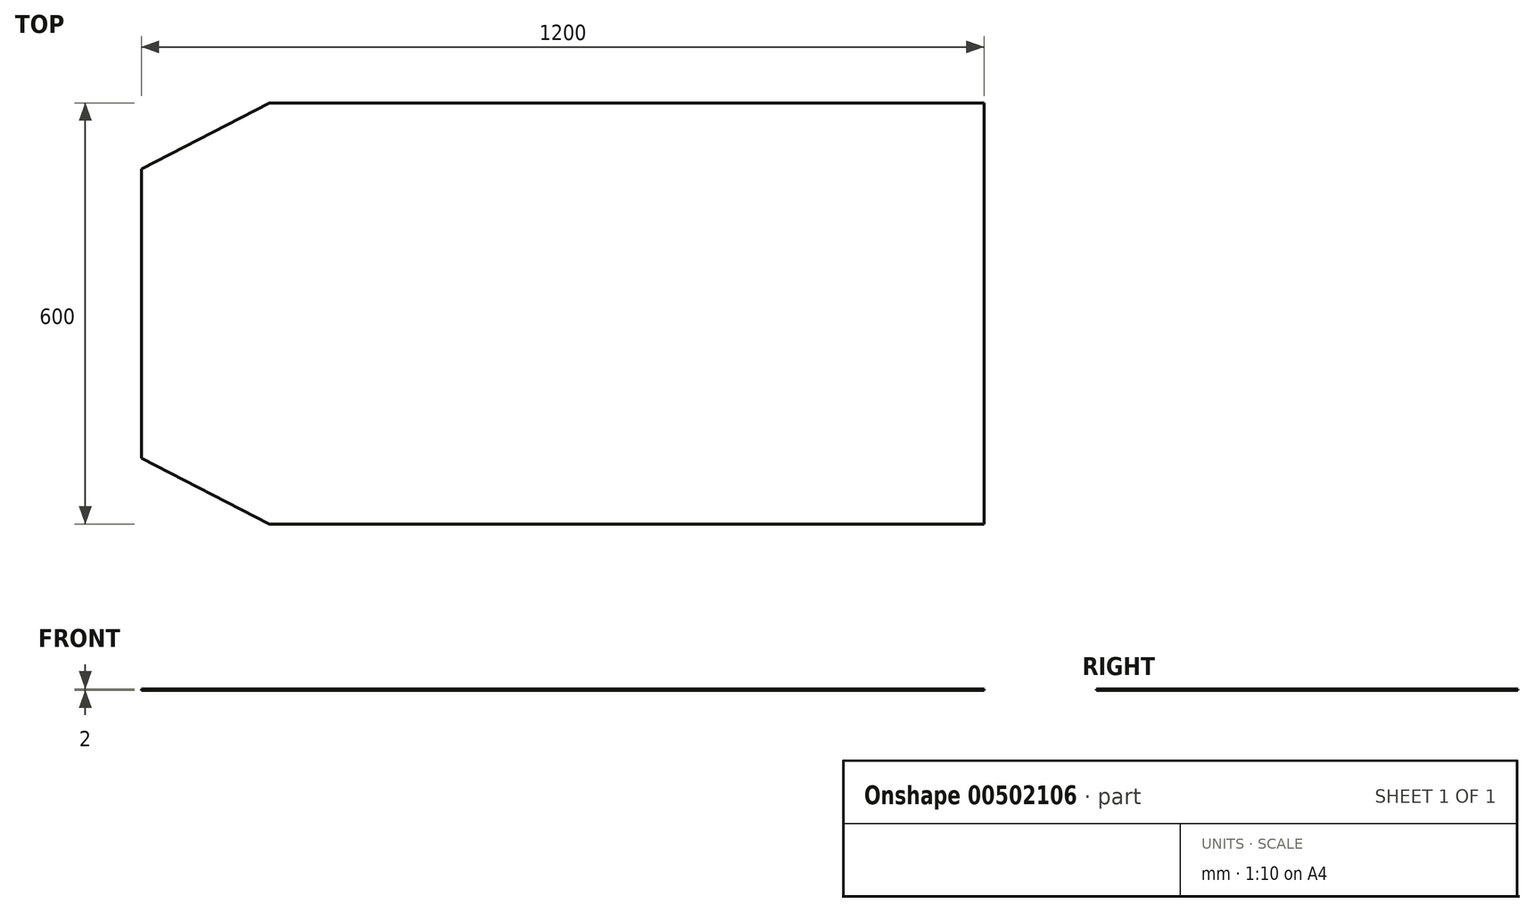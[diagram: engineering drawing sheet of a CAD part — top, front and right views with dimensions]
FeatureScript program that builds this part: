
annotation { "Feature Type Name" : "Feature", "Feature Type Description" : "" }
export const myFeature = defineFeature(function(context is Context, id is Id, definition is map)
    precondition{}
    {
        {
            var Q0;
            Q0=qCreatedBy(makeId("Top.planeOp"),FACE);
            var sketch = newSketch(context, id + "F0", { "sketchPlane" : qUnion([Q0])});
            skLineSegment(sketch, "E0", {"start": v(0, 0) * mm, "end": v(0, 600) * mm});
            skLineSegment(sketch, "E1", {"start": v(0, 600) * mm, "end": v(-1018, 600) * mm});
            skLineSegment(sketch, "E2", {"start": v(-1200, 94) * mm, "end": v(-1200, 506) * mm});
            skLineSegment(sketch, "E3", {"start": v(-1018, 600) * mm, "end": v(-1200, 506) * mm});
            skLineSegment(sketch, "E4.MirrorCS", {"start": v(-1018, 0) * mm, "end": v(-1200, 94) * mm});
            skLineSegment(sketch, "E5", {"start": v(0, 0) * mm, "end": v(-1018, 0) * mm});
            skSolve(sketch);
        }
        {
            var Q0;
            Q0 = qSketchRegion(id + "F0", true);
            extrude(context, id + "F1", {"entities" : qUnion([Q0]), "depth" : 2 * mm});
        }
    });
